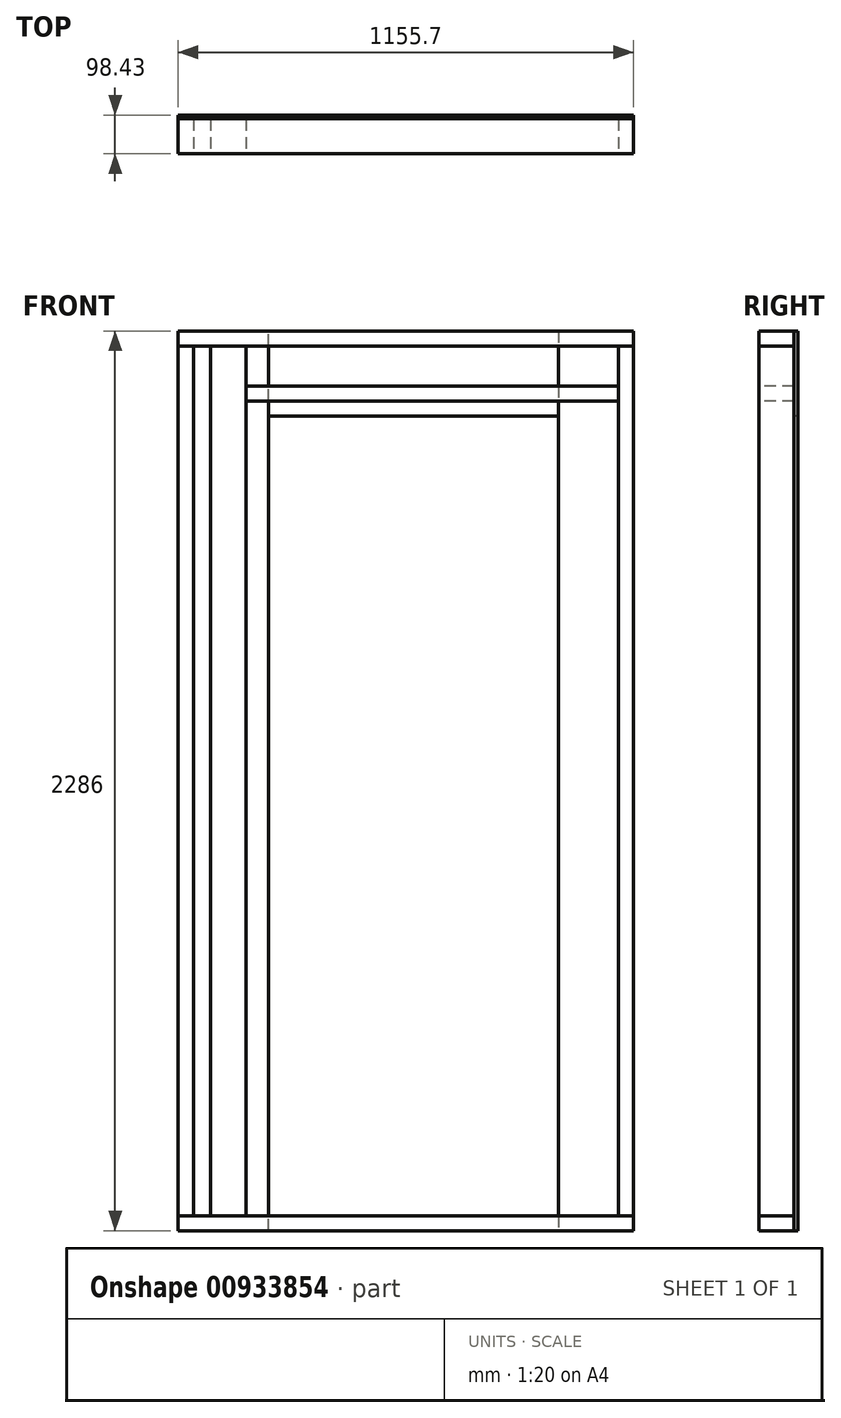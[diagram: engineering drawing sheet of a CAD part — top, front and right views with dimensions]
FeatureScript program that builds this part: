
annotation { "Feature Type Name" : "Feature", "Feature Type Description" : "" }
export const myFeature = defineFeature(function(context is Context, id is Id, definition is map)
    precondition{}
    {
        {
            var Q0;
            Q0=qCreatedBy(makeId("Top.planeOp"),FACE);
            var sketch = newSketch(context, id + "F0", { "sketchPlane" : qUnion([Q0])});
            skLineSegment(sketch, "E0.bottom", {"start": v(0, 0) * mm, "end": v(1155.7, 0) * mm});
            skLineSegment(sketch, "E0.top", {"start": v(0, -88.9) * mm, "end": v(1155.7, -88.9) * mm});
            skLineSegment(sketch, "E0.left", {"start": v(0, 0) * mm, "end": v(0, -88.9) * mm});
            skLineSegment(sketch, "E0.right", {"start": v(1155.7, 0) * mm, "end": v(1155.7, -88.9) * mm});
            skSolve(sketch);
        }
        {
            var Q0;
            Q0=qSketchRegion(id+"F0",true);
            extrude(context, id + "F1", {"entities" : qUnion([Q0]), "depth" : 38.1 * mm, "offsetDistance" : 25.4 * mm});
        }
        {
            var Q0;
            Q0=makeQuery(id+"F1.opExtrude","CAP_FACE",FACE,{"disambiguationData":[OSD([sQuery(id+"F0.wireOp",EDGE,"E0.bottom"),sQuery(id+"F0.wireOp",EDGE,"E0.top"),sQuery(id+"F0.wireOp",EDGE,"E0.left"),sQuery(id+"F0.wireOp",EDGE,"E0.right")])],"isStart":false});
            var sketch = newSketch(context, id + "F2", { "sketchPlane" : qUnion([Q0])});
            skLineSegment(sketch, "E1.bottom", {"start": v(0, 0) * mm, "end": v(38.1, 0) * mm});
            skLineSegment(sketch, "E1.top", {"start": v(0, -88.9) * mm, "end": v(38.1, -88.9) * mm});
            skLineSegment(sketch, "E1.left", {"start": v(0, 0) * mm, "end": v(0, -88.9) * mm});
            skLineSegment(sketch, "E1.right", {"start": v(38.1, 0) * mm, "end": v(38.1, -88.9) * mm});
            skLineSegment(sketch, "E2.bottom", {"start": v(1155.7, 0) * mm, "end": v(1117.6, 0) * mm});
            skLineSegment(sketch, "E2.top", {"start": v(1155.7, -88.9) * mm, "end": v(1117.6, -88.9) * mm});
            skLineSegment(sketch, "E2.left", {"start": v(1155.7, 0) * mm, "end": v(1155.7, -88.9) * mm});
            skLineSegment(sketch, "E2.right", {"start": v(1117.6, 0) * mm, "end": v(1117.6, -88.9) * mm});
            skLineSegment(sketch, "E3.bottom", {"start": v(82.55, 0) * mm, "end": v(171.45, 0) * mm});
            skLineSegment(sketch, "E3.top", {"start": v(82.55, -88.9) * mm, "end": v(171.45, -88.9) * mm});
            skLineSegment(sketch, "E3.left", {"start": v(82.55, 0) * mm, "end": v(82.55, -88.9) * mm});
            skLineSegment(sketch, "E3.right", {"start": v(171.45, 0) * mm, "end": v(171.45, -88.9) * mm});
            skSolve(sketch);
        }
        {
            var Q0;
            Q0=qSketchRegion(id+"F2",true);
            extrude(context, id + "F3", {"entities" : qUnion([Q0]), "depth" : 2209.8 * mm, "offsetDistance" : 25.4 * mm});
        }
        {
            var Q0;
            Q0=makeQuery(id+"F3.opExtrude","CAP_FACE",FACE,{"disambiguationData":[OSD([sQuery(id+"F2.wireOp",EDGE,"E2.bottom"),sQuery(id+"F2.wireOp",EDGE,"E2.top"),sQuery(id+"F2.wireOp",EDGE,"E2.left"),sQuery(id+"F2.wireOp",EDGE,"E2.right")])],"isStart":false});
            var sketch = newSketch(context, id + "F4", { "sketchPlane" : qUnion([Q0])});
            skLineSegment(sketch, "E4.bottom", {"start": v(1155.7, -88.9) * mm, "end": v(0, -88.9) * mm});
            skLineSegment(sketch, "E4.top", {"start": v(1155.7, 0) * mm, "end": v(0, 0) * mm});
            skLineSegment(sketch, "E4.left", {"start": v(1155.7, -88.9) * mm, "end": v(1155.7, 0) * mm});
            skLineSegment(sketch, "E4.right", {"start": v(0, -88.9) * mm, "end": v(0, 0) * mm});
            skSolve(sketch);
        }
        {
            var Q0;
            Q0=qSketchRegion(id+"F4",true);
            extrude(context, id + "F5", {"entities" : qUnion([Q0]), "depth" : 38.1 * mm, "offsetDistance" : 25.4 * mm});
        }
        {
            var Q0;
            Q0=makeQuery(id+"F5.opExtrude","SWEPT_FACE",FACE,{"disambiguationData":[OSD([sQuery(id+"F4.wireOp",EDGE,"E4.top")])]});
            var sketch = newSketch(context, id + "F6", { "sketchPlane" : qUnion([Q0])});
            skLineSegment(sketch, "E5.bottom", {"start": v(-1155.7, 2286) * mm, "end": v(-965.2, 2286) * mm});
            skLineSegment(sketch, "E5.top", {"start": v(-1155.7, 0) * mm, "end": v(-965.2, 0) * mm});
            skLineSegment(sketch, "E5.left", {"start": v(-1155.7, 2286) * mm, "end": v(-1155.7, 0) * mm});
            skLineSegment(sketch, "E5.right", {"start": v(-965.2, 2286) * mm, "end": v(-965.2, 0) * mm});
            skLineSegment(sketch, "E6.bottom", {"start": v(0, 0) * mm, "end": v(-228.6, 0) * mm});
            skLineSegment(sketch, "E6.top", {"start": v(0, 2286) * mm, "end": v(-228.6, 2286) * mm});
            skLineSegment(sketch, "E6.left", {"start": v(0, 0) * mm, "end": v(0, 2286) * mm});
            skLineSegment(sketch, "E6.right", {"start": v(-228.6, 0) * mm, "end": v(-228.6, 2286) * mm});
            skSolve(sketch);
        }
        {
            var Q0;
            Q0=qSketchRegion(id+"F6",true);
            extrude(context, id + "F7", {"entities" : qUnion([Q0]), "depth" : 9.52 * mm, "offsetDistance" : 25.4 * mm});
        }
        {
            var Q0;
            Q0=makeQuery(id+"F5.opExtrude","SWEPT_FACE",FACE,{"disambiguationData":[OSD([sQuery(id+"F4.wireOp",EDGE,"E4.top")])]});
            var sketch = newSketch(context, id + "F8", { "sketchPlane" : qUnion([Q0])});
            skLineSegment(sketch, "E7.bottom", {"start": v(-965.2, 2286) * mm, "end": v(-228.6, 2286) * mm});
            skLineSegment(sketch, "E7.top", {"start": v(-965.2, 2070.1) * mm, "end": v(-228.6, 2070.1) * mm});
            skLineSegment(sketch, "E7.left", {"start": v(-965.2, 2286) * mm, "end": v(-965.2, 2070.1) * mm});
            skLineSegment(sketch, "E7.right", {"start": v(-228.6, 2286) * mm, "end": v(-228.6, 2070.1) * mm});
            skSolve(sketch);
        }
        {
            var Q0;
            Q0=qSketchRegion(id+"F8",true);
            extrude(context, id + "F9", {"entities" : qUnion([Q0]), "depth" : 9.52 * mm, "offsetDistance" : 25.4 * mm});
        }
        {
            var Q0;
            Q0=makeQuery(id+"F3.opExtrude","SWEPT_FACE",FACE,{"disambiguationData":[OSD([sQuery(id+"F2.wireOp",EDGE,"E3.right")])]});
            var sketch = newSketch(context, id + "F10", { "sketchPlane" : qUnion([Q0])});
            skLineSegment(sketch, "E8.bottom", {"start": v(0, 2146.3) * mm, "end": v(-88.9, 2146.3) * mm});
            skLineSegment(sketch, "E8.top", {"start": v(0, 2108.2) * mm, "end": v(-88.9, 2108.2) * mm});
            skLineSegment(sketch, "E8.left", {"start": v(0, 2146.3) * mm, "end": v(0, 2108.2) * mm});
            skLineSegment(sketch, "E8.right", {"start": v(-88.9, 2146.3) * mm, "end": v(-88.9, 2108.2) * mm});
            skSolve(sketch);
        }
        {
            var Q0;
            Q0 = qSketchRegion(id + "F10", true);
            extrude(context, id + "F11", {"entities" : qUnion([Q0]), "depth" : 946.15 * mm, "offsetDistance" : 25.4 * mm});
        }
    });
